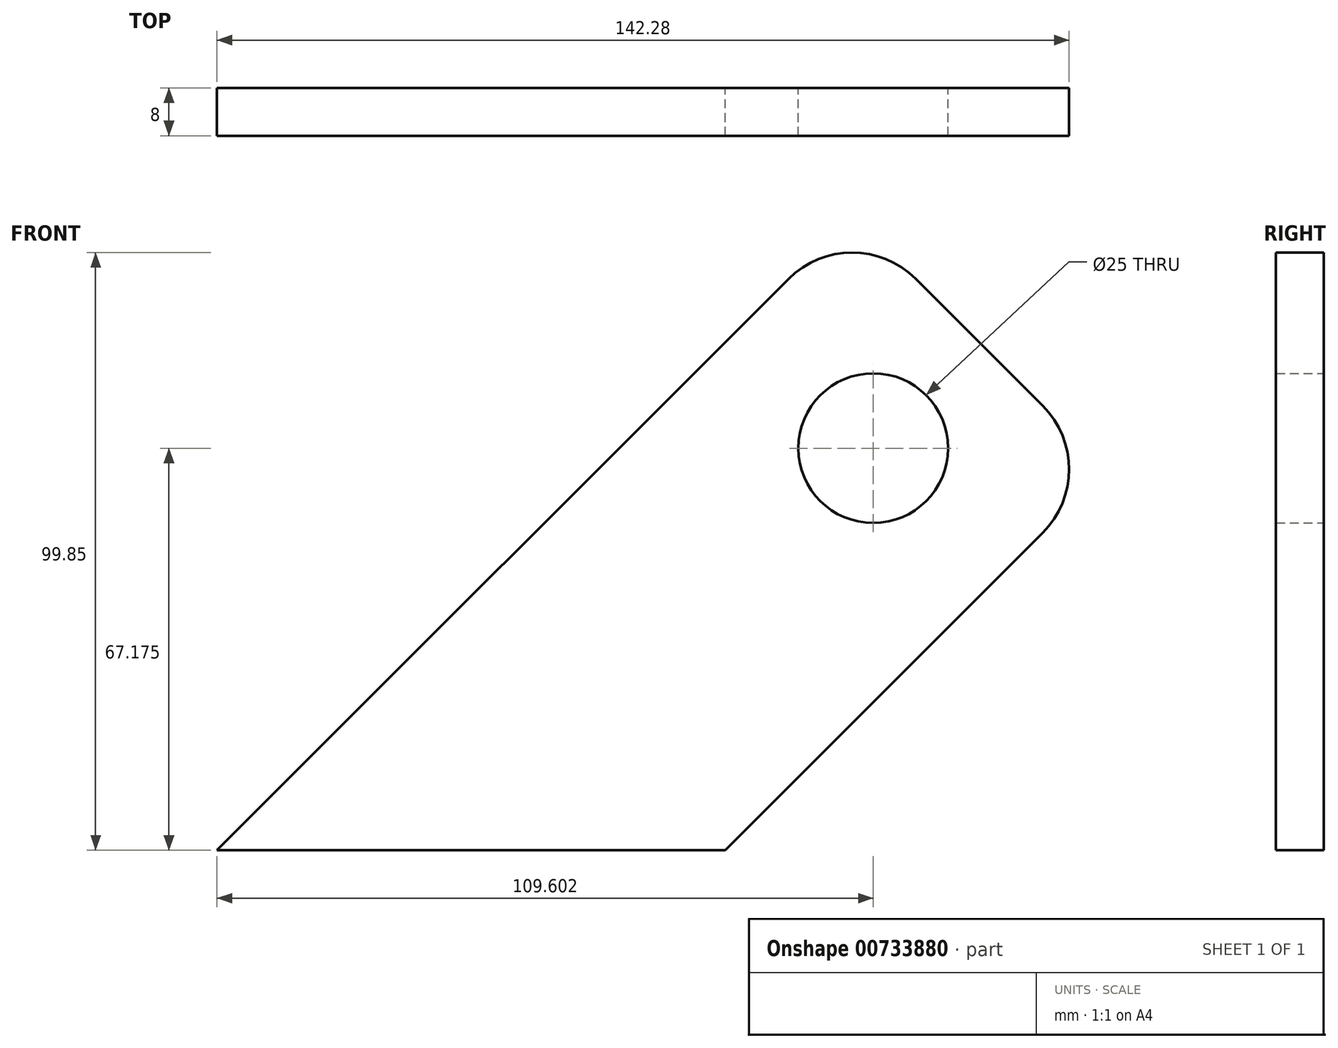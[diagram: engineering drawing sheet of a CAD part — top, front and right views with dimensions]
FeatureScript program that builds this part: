
annotation { "Feature Type Name" : "Feature", "Feature Type Description" : "" }
export const myFeature = defineFeature(function(context is Context, id is Id, definition is map)
    precondition{}
    {
        {
            var Q0;
            Q0=qCreatedBy(makeId("Front.planeOp"),FACE);
            var sketch = newSketch(context, id + "F0", { "sketchPlane" : qUnion([Q0])});
            skLineSegment(sketch, "E0", {"start": v(0, 0) * mm, "end": v(106.07, 106.07) * mm});
            skLineSegment(sketch, "E1", {"start": v(106.07, 106.07) * mm, "end": v(148.5, 63.64) * mm});
            skLineSegment(sketch, "E2", {"start": v(148.5, 63.64) * mm, "end": v(84.85, 0) * mm});
            skLineSegment(sketch, "E3", {"start": v(84.85, 0) * mm, "end": v(0, 0) * mm});
            skCircle(sketch, "E4", {"center": v(109.6, 67.18) * mm, "radius": 12.5 * mm});
            skSolve(sketch);
        }
        {
            var Q0;
            Q0=makeQuery(id+"F0.imprint","IMPRINT",FACE,{"disambiguationData":[TD([[makeQuery(id+"F0.imprint","IMPRINT",EDGE,{"derivedFrom":sQuery(id+"F0.wireOp",EDGE,"E0")}),-1.0]])]});
            extrude(context, id + "F1", {"entities" : qUnion([Q0]), "depth" : 8 * mm, "offsetDistance" : 25 * mm});
        }
        {
            var Q0;
            Q0=makeQuery(id+"F1.opExtrude","SWEPT_EDGE",EDGE,{"disambiguationData":[OSD([sQuery(id+"F0.wireOp",EDGE,"E0"),sQuery(id+"F0.wireOp",EDGE,"E1")])]});
            fillet(context, id + "F2", {"entities" : qUnion([Q0]), "radius" : 15 * mm, "tangentPropagation" : true, "allowEdgeOverflow" : false});
        }
        {
            var Q0;
            Q0=makeQuery(id+"F1.opExtrude","SWEPT_EDGE",EDGE,{"disambiguationData":[OSD([sQuery(id+"F0.wireOp",EDGE,"E1"),sQuery(id+"F0.wireOp",EDGE,"E2")])]});
            fillet(context, id + "F3", {"entities" : qUnion([Q0]), "radius" : 15 * mm, "tangentPropagation" : true, "allowEdgeOverflow" : false});
        }
    });
